# Revit family: Revolving-Door-Stanley-3500AG_Series
name_source: partatom
category: Doors
revit_build: Autodesk Revit 2013 (Build: 20130531_2115(x64)
units: mm (PartAtom-declared; Revit-internal decimal feet)

## types (2) — shared parameters
Appear In Schedule = No
Assembly Code = C1020210
CTRL Frame Opening Width = 50 "
Description = 3 or 4 Panel Revolving Door
Frame Opening Width = 48 "
Frame Width = 3 "
Hardware Finish = Metal - Stanley - Aluminum - Anodized - Clear CL2
Head Rail = 3 "
Manufacturer = Stanley Access Technologies
Model = 3500 Series Revolving Door
Opening Thickness Offset = 0.125 "
Panel Finish = Metal - Stanley - Aluminum - Anodized - Clear CL2
Product Page URL = http://www.stanleyaccesstechnologies.com
Type Comments = Manual
URL = http://www.stanleyaccess.com
Wall Closure = By host

## per-type parameters (varying)
| type | Panel Type |
| 4 Panel | Door-Panel-Stanley-Glass-Full-Revolving_4_3500 |
| 3 Panel | Door-Panel-Stanley-Glass-Full-Revolving_3_3500 |

## geometry (parser evidence)
native form markers: Blend x22, Sweep x7
no freeform markers — native parametric forms only
